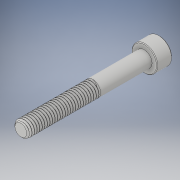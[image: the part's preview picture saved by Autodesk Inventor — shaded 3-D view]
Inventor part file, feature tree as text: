
AUTODESK INVENTOR PART (.ipt)
format: ipt  version: 2018 (Build 220112000, 112)  size: 937,984 bytes
history: native  units: in
note: dims shown in document units (in); Inventor stores cm internally (conversion verified against a paired STEP export)
features: chamfer x1
ambient origin geometry x8: Origin, YZ Plane, XZ Plane, XY Plane, X Axis, Y Axis, Z Axis, Center Point
bodies: Solid1 (feature_tree)
feature tree (1):
  chamfer  "Chamfer2"  [1 undecoded]
note: 1 required parameter value undecoded (feature->parameter linkage not recoverable at this tier; creation-order binding heuristic only, values carry confidence <= 0.55)
